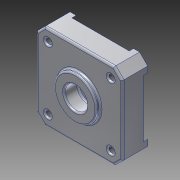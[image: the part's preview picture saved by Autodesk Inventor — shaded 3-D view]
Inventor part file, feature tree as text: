
AUTODESK INVENTOR PART (.ipt)
format: ipt  version: 2016 (Build 200138000, 138)  size: 225,792 bytes
history: native  units: mm
features: extrude x4, thread x4, sketch x4, hole x3, fillet x2, pattern_linear x1
ambient origin geometry x8: Origin, YZ Plane, XZ Plane, XY Plane, X Axis, Y Axis, Z Axis, Center Point
bodies: Solid1 (feature_tree)
feature tree (18):
  extrude  "Extrusion1"  Depth=42.3mm
  extrude  "Extrusion2"  Depth=10.5mm
  extrude  "Extrusion3"  Depth=10.5mm TaperAngle=0.0deg
  hole  "Hole1"  [1 undecoded]
  hole  "Hole2"  [1 undecoded]
  pattern_linear  "Rectangular Pattern1"  Spacing1=5.65mm  [1 undecoded]
  hole  "Hole3"  [1 undecoded]
  fillet  "Fillet1"  Radius=20.0mm
  extrude  "Extrusion4"  Depth=10.0mm
  fillet  "Fillet4"  Radius=1.0mm
  thread  "Thread1"  [1 undecoded]
  thread  "Thread2"  [1 undecoded]
  thread  "Thread3"  [1 undecoded]
  thread  "Thread4"  [1 undecoded]
  sketch  "Sketch1"  dims[d0=42.3mm d1=42.3mm]
  sketch  "Sketch2"  dims[d2=10.5mm d3=0.0mm d4=5.657mm]
  sketch  "Sketch3"  dims[d5=135.0deg d6=10.5mm d7=0.0mm]
  sketch  "Sketch4"  dims[d8=2.121mm d9=2.121mm d10=0.0mm d11=21.15mm d12=21.15mm d13=5.0mm d14=6.0mm d15=4.0mm d16=2.0mm d17=90.0deg d18=8.0mm d19=20.594885mm d20=5.65mm d21=5.65mm d22=3.0mm d23=6.0mm d24=4.0mm d25=2.0mm d26=90.0deg d27=8.0mm d28=20.594885mm d29=20.0mm d31=31.0mm d32=20.0mm d34=31.0mm d35=21.15mm d36=21.15mm d37=11.0mm d38=6.0mm d39=4.0mm d40=2.0mm d41=90.0deg d42=5.0mm d43=0.0mm d59=1.0mm d62=21.0mm d63=2.0mm d64=0.0mm d65=0.75mm d66=10.0mm d67=0.0mm d68=10.0mm d69=0.0mm d70=10.0mm d71=0.0mm d72=10.0mm d73=0.0mm]
note: 8 required parameter values undecoded (feature->parameter linkage not recoverable at this tier; creation-order binding heuristic only, values carry confidence <= 0.55)
